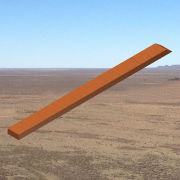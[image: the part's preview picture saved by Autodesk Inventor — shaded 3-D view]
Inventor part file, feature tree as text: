
AUTODESK INVENTOR PART (.ipt)
format: ipt  version: 2013 SP2 (Build 170200200, 200)  size: 140,288 bytes
history: native  units: in
note: dims shown in document units (in); Inventor stores cm internally (conversion verified against a paired STEP export)
features: sketch x2, extrude x1, hole x1
ambient origin geometry x8: Origin, YZ Plane, XZ Plane, XY Plane, X Axis, Y Axis, Z Axis, Center Point
bodies: Solid1 (feature_tree)
feature tree (4):
  extrude  "Extrusion1"  Depth=48.8in
  hole  "Hole1"  [1 undecoded]
  sketch  "Sketch1"  dims[d0=1.5in d1=48.8in]
  sketch  "Sketch2"  dims[d3=0.2577in d4=3.5in d5=0.0in d6=1.0in d7=0.7874in d9=1.5in d10=0.3937in d12=1.0in d14=0.25in d15=0.75in d16=0.375in d17=0.25in d18=0.5635in d19=1.0in d20=0.8108in]
note: 1 required parameter value undecoded (feature->parameter linkage not recoverable at this tier; creation-order binding heuristic only, values carry confidence <= 0.55)
